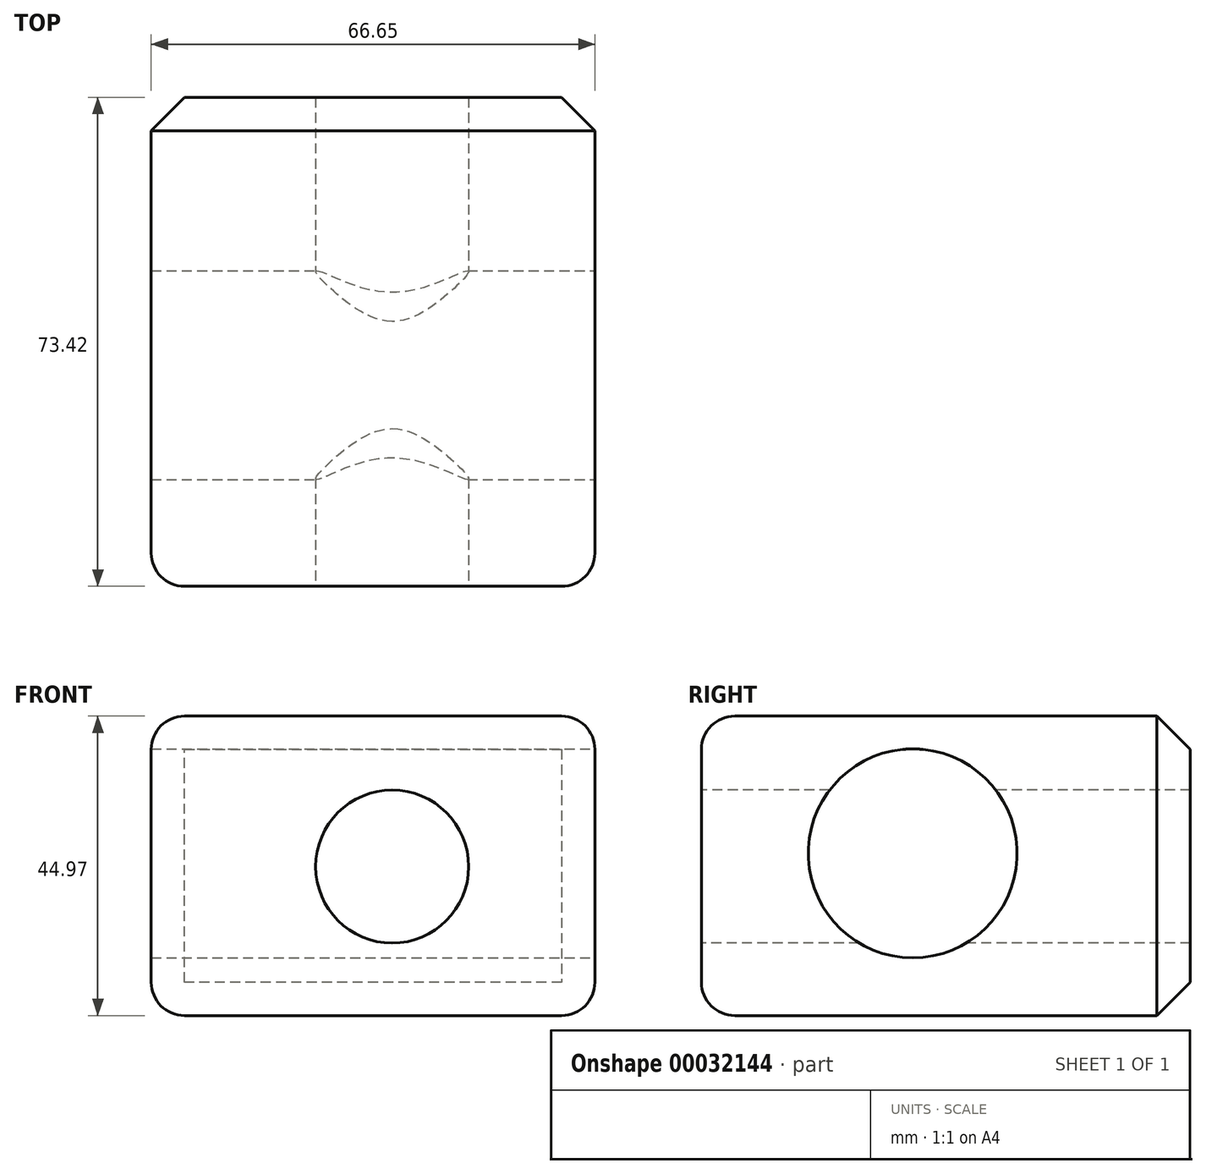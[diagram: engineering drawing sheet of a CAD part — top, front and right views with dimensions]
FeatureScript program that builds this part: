
annotation { "Feature Type Name" : "Feature", "Feature Type Description" : "" }
export const myFeature = defineFeature(function(context is Context, id is Id, definition is map)
    precondition{}
    {
        {
            var Q0;
            Q0=qCreatedBy(makeId("Top.planeOp"),FACE);
            var sketch = newSketch(context, id + "F0", { "sketchPlane" : qUnion([Q0])});
            skLineSegment(sketch, "E0.bottom", {"start": v(-36.2, -31.73) * mm, "end": v(30.45, -31.73) * mm});
            skLineSegment(sketch, "E0.top", {"start": v(-36.2, 41.7) * mm, "end": v(30.45, 41.7) * mm});
            skLineSegment(sketch, "E0.left", {"start": v(-36.2, -31.73) * mm, "end": v(-36.2, 41.7) * mm});
            skLineSegment(sketch, "E0.right", {"start": v(30.45, -31.73) * mm, "end": v(30.45, 41.7) * mm});
            skSolve(sketch);
        }
        {
            var Q0;
            Q0=makeQuery(id+"F0.imprint","IMPRINT",FACE,{"disambiguationData":[TD([[makeQuery(id+"F0.imprint","IMPRINT",EDGE,{"derivedFrom":sQuery(id+"F0.wireOp",EDGE,"E0.bottom")}),1.0]])]});
            extrude(context, id + "F1", {"entities" : qUnion([Q0]), "depth" : 44.97 * mm});
        }
        {
            var Q0;
            Q0=makeQuery(id+"F1.opExtrude","SWEPT_FACE",FACE,{"disambiguationData":[OSD([sQuery(id+"F0.wireOp",EDGE,"E0.bottom")])]});
            extrude(context, id + "F2", {"entities" : qUnion([Q0]), "operationType" : NewBodyOperationType.ADD, "oppositeDirection" : true, "depth" : 8.1 * mm});
        }
        {
            var Q0;
            Q0=makeQuery(id+"F1.opExtrude","SWEPT_FACE",FACE,{"disambiguationData":[OSD([sQuery(id+"F0.wireOp",EDGE,"E0.right")])]});
            var sketch = newSketch(context, id + "F3", { "sketchPlane" : qUnion([Q0])});
            skCircle(sketch, "E1", {"center": v(0, 24.36) * mm, "radius": 15.69 * mm});
            skSolve(sketch);
        }
        {
            var Q0;
            Q0=makeQuery(id+"F3.imprint","IMPRINT",FACE,{"disambiguationData":[TD([[makeQuery(id+"F3.imprint","IMPRINT",EDGE,{"derivedFrom":sQuery(id+"F3.wireOp",EDGE,"E1")}),1.0]])]});
            extrude(context, id + "F4", {"entities" : qUnion([Q0]), "operationType" : NewBodyOperationType.REMOVE, "endBound" : BoundingType.UP_TO_NEXT, "oppositeDirection" : true, "depth" : 101.7 * mm});
        }
        {
            var Q0;
            Q0=makeQuery(id+"F1.opExtrude","SWEPT_FACE",FACE,{"disambiguationData":[OSD([sQuery(id+"F0.wireOp",EDGE,"E0.bottom")])]});
            var sketch = newSketch(context, id + "F5", { "sketchPlane" : qUnion([Q0])});
            skCircle(sketch, "E2", {"center": v(0, 22.37) * mm, "radius": 11.49 * mm});
            skSolve(sketch);
        }
        {
            var Q0;
            Q0=makeQuery(id+"F5.imprint","IMPRINT",FACE,{"disambiguationData":[TD([[makeQuery(id+"F5.imprint","IMPRINT",EDGE,{"derivedFrom":sQuery(id+"F5.wireOp",EDGE,"E2")}),1.0]])]});
            extrude(context, id + "F6", {"entities" : qUnion([Q0]), "operationType" : NewBodyOperationType.REMOVE, "endBound" : BoundingType.THROUGH_ALL, "oppositeDirection" : true, "depth" : 71.54 * mm});
        }
        {
            var Q0;
            Q0=makeQuery(id+"F1.opExtrude","CAP_EDGE",EDGE,{"disambiguationData":[OSD([sQuery(id+"F0.wireOp",EDGE,"E0.bottom")])],"isStart":false});
            var Q1;
            Q1=makeQuery(id+"F1.opExtrude","SWEPT_EDGE",EDGE,{"disambiguationData":[OSD([sQuery(id+"F0.wireOp",EDGE,"E0.bottom"),sQuery(id+"F0.wireOp",EDGE,"E0.left")])]});
            var Q2;
            Q2=makeQuery(id+"F1.opExtrude","CAP_EDGE",EDGE,{"disambiguationData":[OSD([sQuery(id+"F0.wireOp",EDGE,"E0.bottom")])],"isStart":true});
            var Q3;
            Q3=makeQuery(id+"F1.opExtrude","SWEPT_EDGE",EDGE,{"disambiguationData":[OSD([sQuery(id+"F0.wireOp",EDGE,"E0.bottom"),sQuery(id+"F0.wireOp",EDGE,"E0.right")])]});
            fillet(context, id + "F7", {"entities" : qUnion([Q0, Q1, Q2, Q3]), "radius" : 5 * mm, "tangentPropagation" : true, "allowEdgeOverflow" : false});
        }
        {
            var Q0;
            Q0=makeQuery(id+"F1.opExtrude","CAP_EDGE",EDGE,{"disambiguationData":[OSD([sQuery(id+"F0.wireOp",EDGE,"E0.right")])],"isStart":false});
            var Q1;
            Q1=makeQuery(id+"F1.opExtrude","CAP_EDGE",EDGE,{"disambiguationData":[OSD([sQuery(id+"F0.wireOp",EDGE,"E0.right")])],"isStart":true});
            var Q2;
            Q2=makeQuery(id+"F1.opExtrude","CAP_EDGE",EDGE,{"disambiguationData":[OSD([sQuery(id+"F0.wireOp",EDGE,"E0.left")])],"isStart":false});
            var Q3;
            Q3=makeQuery(id+"F1.opExtrude","CAP_EDGE",EDGE,{"disambiguationData":[OSD([sQuery(id+"F0.wireOp",EDGE,"E0.left")])],"isStart":true});
            fillet(context, id + "F8", {"entities" : qUnion([Q0, Q1, Q2, Q3]), "radius" : 5 * mm, "tangentPropagation" : true, "allowEdgeOverflow" : false});
        }
        {
            var Q0;
            Q0=makeQuery(id+"F1.opExtrude","CAP_EDGE",EDGE,{"disambiguationData":[OSD([sQuery(id+"F0.wireOp",EDGE,"E0.top")])],"isStart":false});
            var Q1;
            Q1=makeQuery(id+"F8.opFillet","BLEND_EDGE",EDGE,{"blendedFrom":[makeQuery(id+"F1.opExtrude","CAP_EDGE",EDGE,{"disambiguationData":[OSD([sQuery(id+"F0.wireOp",EDGE,"E0.left")])],"isStart":false}),makeQuery(id+"F1.opExtrude","SWEPT_FACE",FACE,{"disambiguationData":[OSD([sQuery(id+"F0.wireOp",EDGE,"E0.top")])]})],"blendedInto":[makeQuery(id+"F1.opExtrude","SWEPT_FACE",FACE,{"disambiguationData":[OSD([sQuery(id+"F0.wireOp",EDGE,"E0.top")])]})]});
            var Q2;
            Q2=makeQuery(id+"F1.opExtrude","SWEPT_EDGE",EDGE,{"disambiguationData":[OSD([sQuery(id+"F0.wireOp",EDGE,"E0.top"),sQuery(id+"F0.wireOp",EDGE,"E0.left")])]});
            var Q3;
            Q3=makeQuery(id+"F8.opFillet","BLEND_EDGE",EDGE,{"blendedFrom":[makeQuery(id+"F1.opExtrude","CAP_EDGE",EDGE,{"disambiguationData":[OSD([sQuery(id+"F0.wireOp",EDGE,"E0.left")])],"isStart":true}),makeQuery(id+"F1.opExtrude","SWEPT_FACE",FACE,{"disambiguationData":[OSD([sQuery(id+"F0.wireOp",EDGE,"E0.top")])]})],"blendedInto":[makeQuery(id+"F1.opExtrude","SWEPT_FACE",FACE,{"disambiguationData":[OSD([sQuery(id+"F0.wireOp",EDGE,"E0.top")])]})]});
            var Q4;
            Q4=makeQuery(id+"F1.opExtrude","CAP_EDGE",EDGE,{"disambiguationData":[OSD([sQuery(id+"F0.wireOp",EDGE,"E0.top")])],"isStart":true});
            var Q5;
            Q5=makeQuery(id+"F8.opFillet","BLEND_EDGE",EDGE,{"blendedFrom":[makeQuery(id+"F1.opExtrude","CAP_EDGE",EDGE,{"disambiguationData":[OSD([sQuery(id+"F0.wireOp",EDGE,"E0.right")])],"isStart":true}),makeQuery(id+"F1.opExtrude","SWEPT_FACE",FACE,{"disambiguationData":[OSD([sQuery(id+"F0.wireOp",EDGE,"E0.top")])]})],"blendedInto":[makeQuery(id+"F1.opExtrude","SWEPT_FACE",FACE,{"disambiguationData":[OSD([sQuery(id+"F0.wireOp",EDGE,"E0.top")])]})]});
            var Q6;
            Q6=makeQuery(id+"F1.opExtrude","SWEPT_EDGE",EDGE,{"disambiguationData":[OSD([sQuery(id+"F0.wireOp",EDGE,"E0.top"),sQuery(id+"F0.wireOp",EDGE,"E0.right")])]});
            var Q7;
            Q7=makeQuery(id+"F8.opFillet","BLEND_EDGE",EDGE,{"blendedFrom":[makeQuery(id+"F1.opExtrude","CAP_EDGE",EDGE,{"disambiguationData":[OSD([sQuery(id+"F0.wireOp",EDGE,"E0.right")])],"isStart":false}),makeQuery(id+"F1.opExtrude","SWEPT_FACE",FACE,{"disambiguationData":[OSD([sQuery(id+"F0.wireOp",EDGE,"E0.top")])]})],"blendedInto":[makeQuery(id+"F1.opExtrude","SWEPT_FACE",FACE,{"disambiguationData":[OSD([sQuery(id+"F0.wireOp",EDGE,"E0.top")])]})]});
            chamfer(context, id + "F9", {"entities" : qUnion([Q0, Q1, Q2, Q3, Q4, Q5, Q6, Q7]), "width" : 5 * mm, "tangentPropagation" : true});
        }
    });
